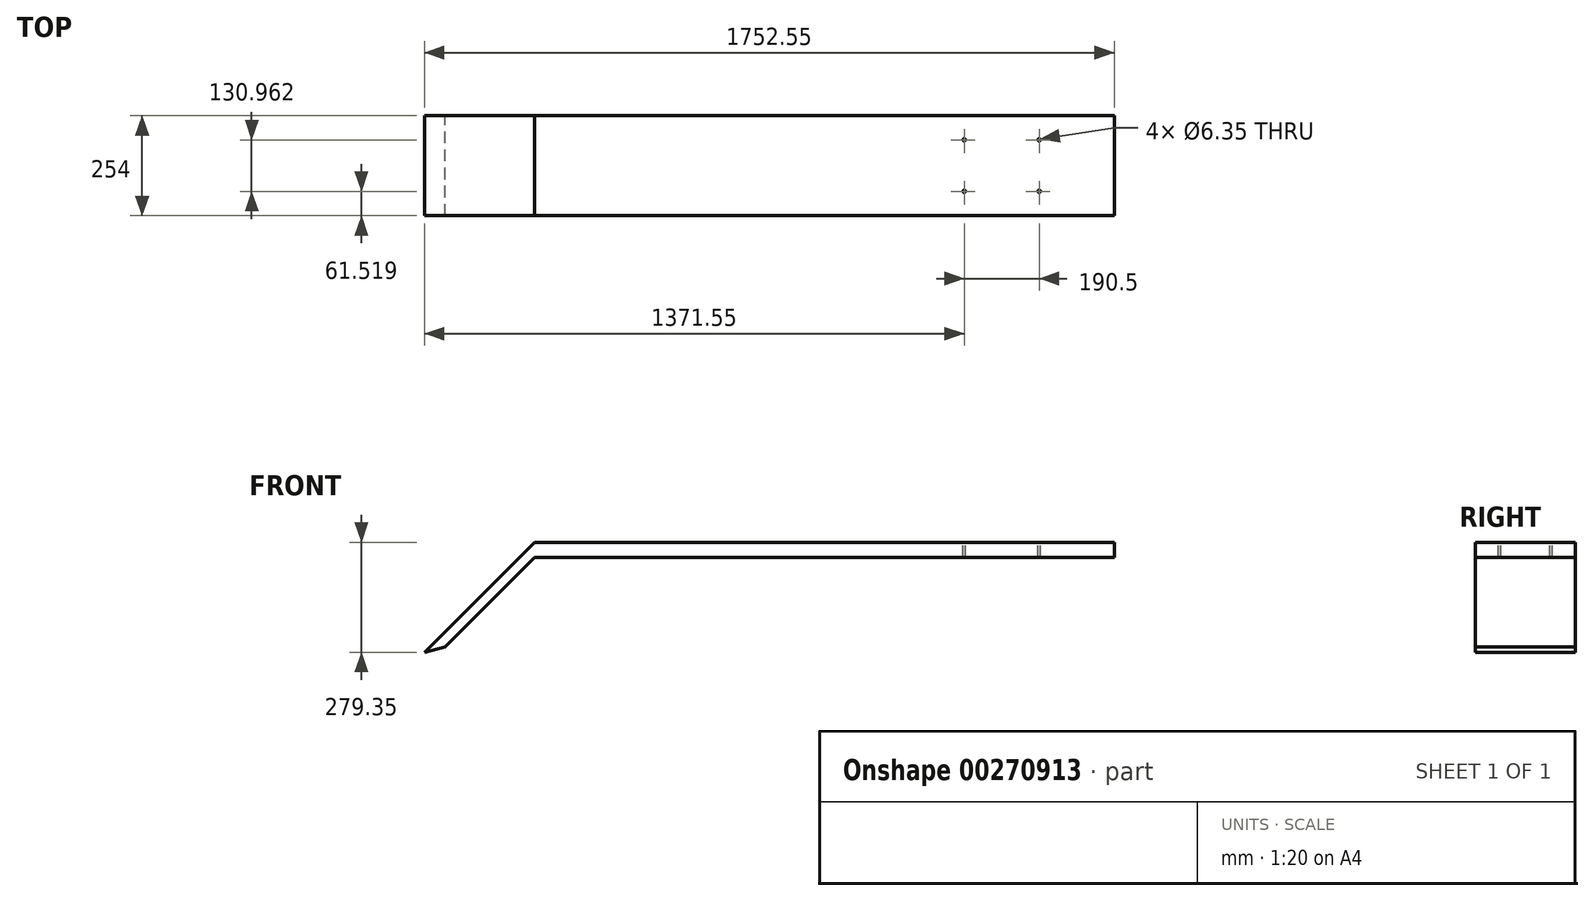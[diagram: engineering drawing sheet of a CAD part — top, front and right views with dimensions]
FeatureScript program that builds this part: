
annotation { "Feature Type Name" : "Feature", "Feature Type Description" : "" }
export const myFeature = defineFeature(function(context is Context, id is Id, definition is map)
    precondition{}
    {
        {
            var Q0;
            Q0=qCreatedBy(makeId("Front.planeOp"),FACE);
            var sketch = newSketch(context, id + "F0", { "sketchPlane" : qUnion([Q0])});
            skLineSegment(sketch, "E0", {"start": v(0, 0) * mm, "end": v(1473.2, 0) * mm});
            skLineSegment(sketch, "E1.0", {"start": v(0, 38.1) * mm, "end": v(1473.2, 38.1) * mm});
            skLineSegment(sketch, "E2", {"start": v(1473.2, 0) * mm, "end": v(1473.2, 38.1) * mm});
            skLineSegment(sketch, "E3", {"start": v(0, 38.1) * mm, "end": v(-279.35, -241.25) * mm});
            skPoint(sketch, "E4.endSnap0", {"position": v(-260.3, -241.25) * mm});
            skLineSegment(sketch, "E5", {"start": v(0, 0) * mm, "end": v(-227.3, -227.3) * mm});
            skLineSegment(sketch, "E6", {"start": v(-279.35, -241.25) * mm, "end": v(-227.3, -227.3) * mm});
            skPoint(sketch, "E4.end.orphan", {"position": v(-260.3, -260.3) * mm});
            skSolve(sketch);
        }
        {
            var Q0;
            Q0=makeQuery(id+"F0.imprint","IMPRINT",FACE,{"disambiguationData":[TD([[makeQuery(id+"F0.imprint","IMPRINT",EDGE,{"derivedFrom":sQuery(id+"F0.wireOp",EDGE,"E0")}),1.0]])]});
            extrude(context, id + "F1", {"entities" : qUnion([Q0]), "depth" : 254 * mm});
        }
        {
            var Q0;
            Q0=makeQuery(id+"F1.opExtrude","SWEPT_FACE",FACE,{"disambiguationData":[OSD([sQuery(id+"F0.wireOp",EDGE,"E1.0")])]});
            var sketch = newSketch(context, id + "F2", { "sketchPlane" : qUnion([Q0])});
            skLineSegment(sketch, "E7", {"start": v(0, 0) * mm, "end": v(0, -254) * mm});
            skLineSegment(sketch, "E8", {"start": v(1473.2, 0) * mm, "end": v(1473.2, -19.34) * mm});
            skLineSegment(sketch, "E9", {"start": v(1473.2, 0) * mm, "end": v(1473.2, -254) * mm});
            skLineSegment(sketch, "E10", {"start": v(1092.2, -254) * mm, "end": v(1282.7, -254) * mm});
            skCircle(sketch, "E11", {"center": v(1092.2, -61.52) * mm, "radius": 3.18 * mm});
            skCircle(sketch, "E12", {"center": v(1092.2, -192.48) * mm, "radius": 3.18 * mm});
            skCircle(sketch, "E13", {"center": v(1282.7, -61.52) * mm, "radius": 3.18 * mm});
            skCircle(sketch, "E14", {"center": v(1282.7, -192.48) * mm, "radius": 3.18 * mm});
            skSolve(sketch);
        }
        {
            var Q0;
            Q0 = qSketchRegion(id + "F2", true);
            extrude(context, id + "F3", {"entities" : qUnion([Q0]), "operationType" : NewBodyOperationType.REMOVE, "oppositeDirection" : true, "depth" : 38.1 * mm});
        }
    });
